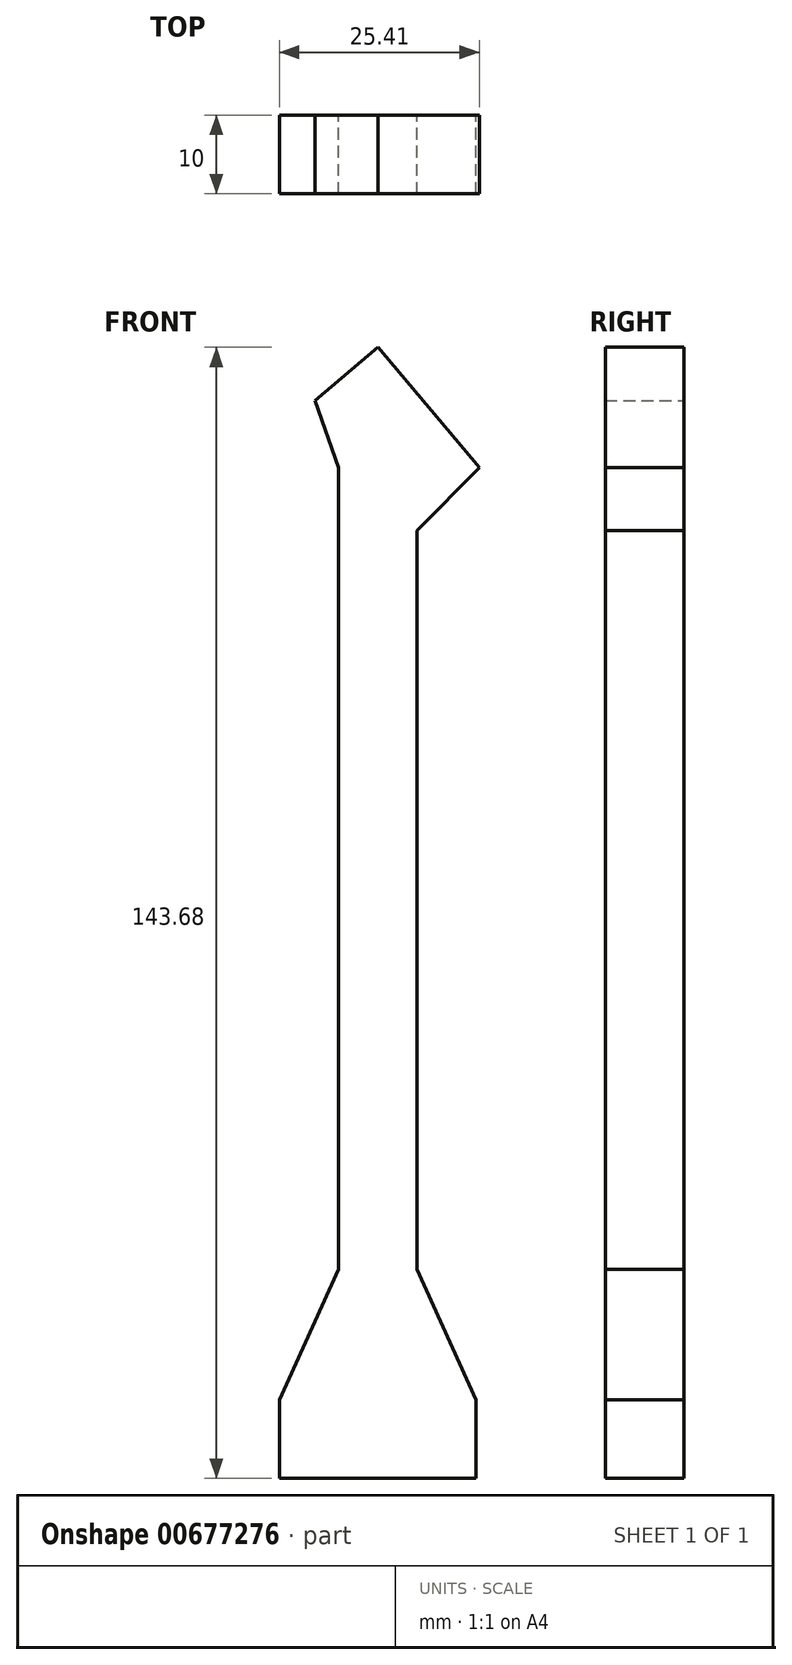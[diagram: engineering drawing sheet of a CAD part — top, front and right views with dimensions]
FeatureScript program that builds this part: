
annotation { "Feature Type Name" : "Feature", "Feature Type Description" : "" }
export const myFeature = defineFeature(function(context is Context, id is Id, definition is map)
    precondition{}
    {
        {
            var Q0;
            Q0=qCreatedBy(makeId("Front.planeOp"),FACE);
            var sketch = newSketch(context, id + "F0", { "sketchPlane" : qUnion([Q0])});
            skLineSegment(sketch, "E0", {"start": v(0, 0) * mm, "end": v(-12.9, 15.28) * mm});
            skLineSegment(sketch, "E1", {"start": v(-12.9, 15.28) * mm, "end": v(-20.9, 8.52) * mm});
            skLineSegment(sketch, "E2", {"start": v(-20.9, 8.52) * mm, "end": v(-17.9, 0) * mm});
            skLineSegment(sketch, "E3", {"start": v(-17.9, 0) * mm, "end": v(-17.9, -101.85) * mm});
            skLineSegment(sketch, "E4", {"start": v(-17.9, -101.85) * mm, "end": v(-25.4, -118.4) * mm});
            skLineSegment(sketch, "E5", {"start": v(-25.4, -118.4) * mm, "end": v(-25.4, -128.4) * mm});
            skLineSegment(sketch, "E6", {"start": v(-25.4, -128.4) * mm, "end": v(-0.4, -128.4) * mm});
            skLineSegment(sketch, "E7", {"start": v(-0.4, -128.4) * mm, "end": v(-0.4, -118.4) * mm});
            skLineSegment(sketch, "E8", {"start": v(-0.4, -118.4) * mm, "end": v(-7.9, -101.85) * mm});
            skLineSegment(sketch, "E9", {"start": v(-7.9, -101.85) * mm, "end": v(-7.9, -8) * mm});
            skLineSegment(sketch, "E10", {"start": v(-7.9, -8) * mm, "end": v(0, 0) * mm});
            skSolve(sketch);
        }
        {
            var Q0;
            Q0 = qSketchRegion(id + "F0", true);
            extrude(context, id + "F1", {"entities" : qUnion([Q0]), "depth" : 10 * mm, "offsetDistance" : 25 * mm});
        }
    });
